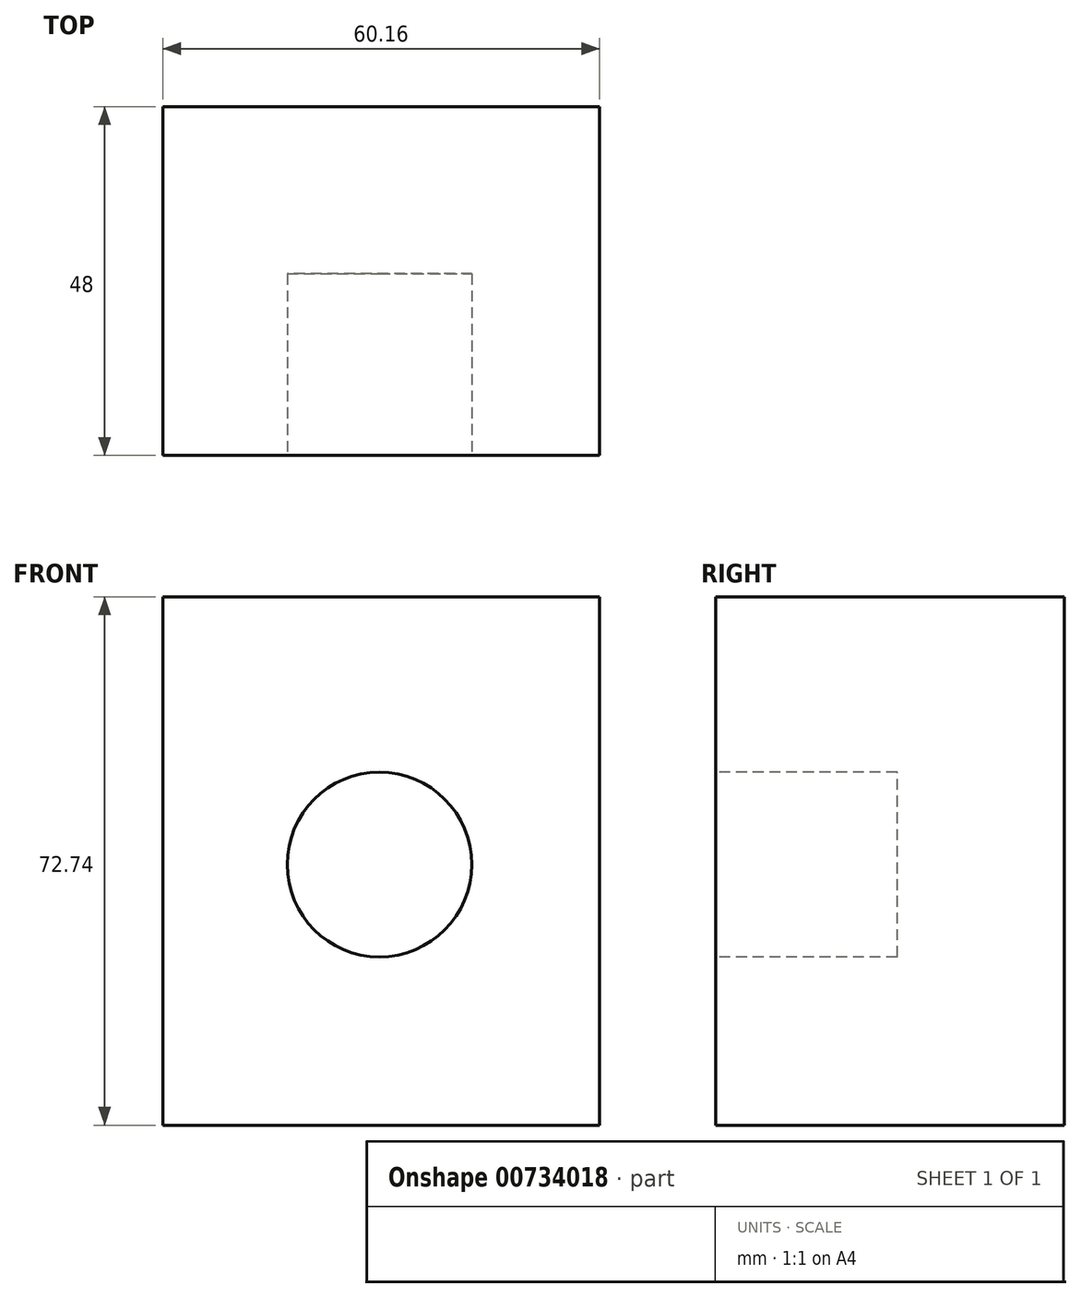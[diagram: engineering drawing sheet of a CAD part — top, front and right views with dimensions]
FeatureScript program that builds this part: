
annotation { "Feature Type Name" : "Feature", "Feature Type Description" : "" }
export const myFeature = defineFeature(function(context is Context, id is Id, definition is map)
    precondition{}
    {
        {
            var Q0;
            Q0=qCreatedBy(makeId("Front.planeOp"),FACE);
            var sketch = newSketch(context, id + "F0", { "sketchPlane" : qUnion([Q0])});
            skLineSegment(sketch, "E0.bottom", {"start": v(0, 0) * mm, "end": v(60.16, 0) * mm});
            skLineSegment(sketch, "E0.top", {"start": v(0, 62.74) * mm, "end": v(60.16, 62.74) * mm});
            skLineSegment(sketch, "E0.left", {"start": v(0, 0) * mm, "end": v(0, 62.74) * mm});
            skLineSegment(sketch, "E0.right", {"start": v(60.16, 0) * mm, "end": v(60.16, 62.74) * mm});
            skSolve(sketch);
        }
        {
            var Q0;
            Q0 = qSketchRegion(id + "F0", true);
            extrude(context, id + "F1", {"entities" : qUnion([Q0]), "depth" : 48 * mm, "offsetDistance" : 25.4 * mm});
        }
        {
            var Q0;
            Q0=makeQuery(id+"F1.opExtrude","SWEPT_FACE",FACE,{"disambiguationData":[OSD([sQuery(id+"F0.wireOp",EDGE,"E0.top")])]});
            extrude(context, id + "F2", {"entities" : qUnion([Q0]), "operationType" : NewBodyOperationType.ADD, "depth" : 10 * mm, "offsetDistance" : 25 * mm});
        }
        {
            var Q0;
            {var subQ0=sQuery(id+"F0.wireOp",EDGE,"E0.top");Q0=makeQuery(id+"F2.boolean.opBoolean","MERGE",FACE,{"derivedFrom":[makeQuery(id+"F1.opExtrude","CAP_FACE",FACE,{"disambiguationData":[OSD([sQuery(id+"F0.wireOp",EDGE,"E0.bottom"),subQ0,sQuery(id+"F0.wireOp",EDGE,"E0.left"),sQuery(id+"F0.wireOp",EDGE,"E0.right")])],"isStart":false}),makeQuery(id+"F2.opExtrude","SWEPT_FACE",FACE,{"disambiguationData":[OSD([subQ0]),TDD([makeQuery(id+"F1.opExtrude","CAP_EDGE",EDGE,{"disambiguationData":[OSD([subQ0])],"isStart":false})])]})]});}
            var sketch = newSketch(context, id + "F3", { "sketchPlane" : qUnion([Q0])});
            skCircle(sketch, "E1", {"center": v(29.86, 35.9) * mm, "radius": 12.72 * mm});
            skSolve(sketch);
        }
        {
            var Q0;
            {var subQ0=sQuery(id+"F0.wireOp",EDGE,"E0.top");Q0=makeQuery(id+"F2.boolean.opBoolean","MERGE",FACE,{"derivedFrom":[makeQuery(id+"F1.opExtrude","CAP_FACE",FACE,{"disambiguationData":[OSD([sQuery(id+"F0.wireOp",EDGE,"E0.bottom"),subQ0,sQuery(id+"F0.wireOp",EDGE,"E0.left"),sQuery(id+"F0.wireOp",EDGE,"E0.right")])],"isStart":false}),makeQuery(id+"F2.opExtrude","SWEPT_FACE",FACE,{"disambiguationData":[OSD([subQ0]),TDD([makeQuery(id+"F1.opExtrude","CAP_EDGE",EDGE,{"disambiguationData":[OSD([subQ0])],"isStart":false})])]})]});}
            var sketch = newSketch(context, id + "F4", { "sketchPlane" : qUnion([Q0])});
            skCircle(sketch, "E2", {"center": v(30.48, 35.9) * mm, "radius": 12.38 * mm});
            skSolve(sketch);
        }
        {
            var Q0;
            Q0=makeQuery(id+"F4.imprint","IMPRINT",FACE,{"disambiguationData":[TD([[makeQuery(id+"F4.imprint","IMPRINT",EDGE,{"derivedFrom":sQuery(id+"F4.wireOp",EDGE,"E2")}),1.0]])]});
            extrude(context, id + "F5", {"entities" : qUnion([Q0]), "operationType" : NewBodyOperationType.ADD, "oppositeDirection" : true, "depth" : 30 * mm, "offsetDistance" : 25 * mm});
        }
        {
            var Q0;
            Q0=makeQuery(id+"F3.imprint","IMPRINT",FACE,{"disambiguationData":[TD([[makeQuery(id+"F3.imprint","IMPRINT",EDGE,{"derivedFrom":sQuery(id+"F3.wireOp",EDGE,"E1")}),1.0]])]});
            extrude(context, id + "F6", {"entities" : qUnion([Q0]), "operationType" : NewBodyOperationType.REMOVE, "oppositeDirection" : true, "depth" : 25 * mm, "offsetDistance" : 25 * mm});
        }
    });
